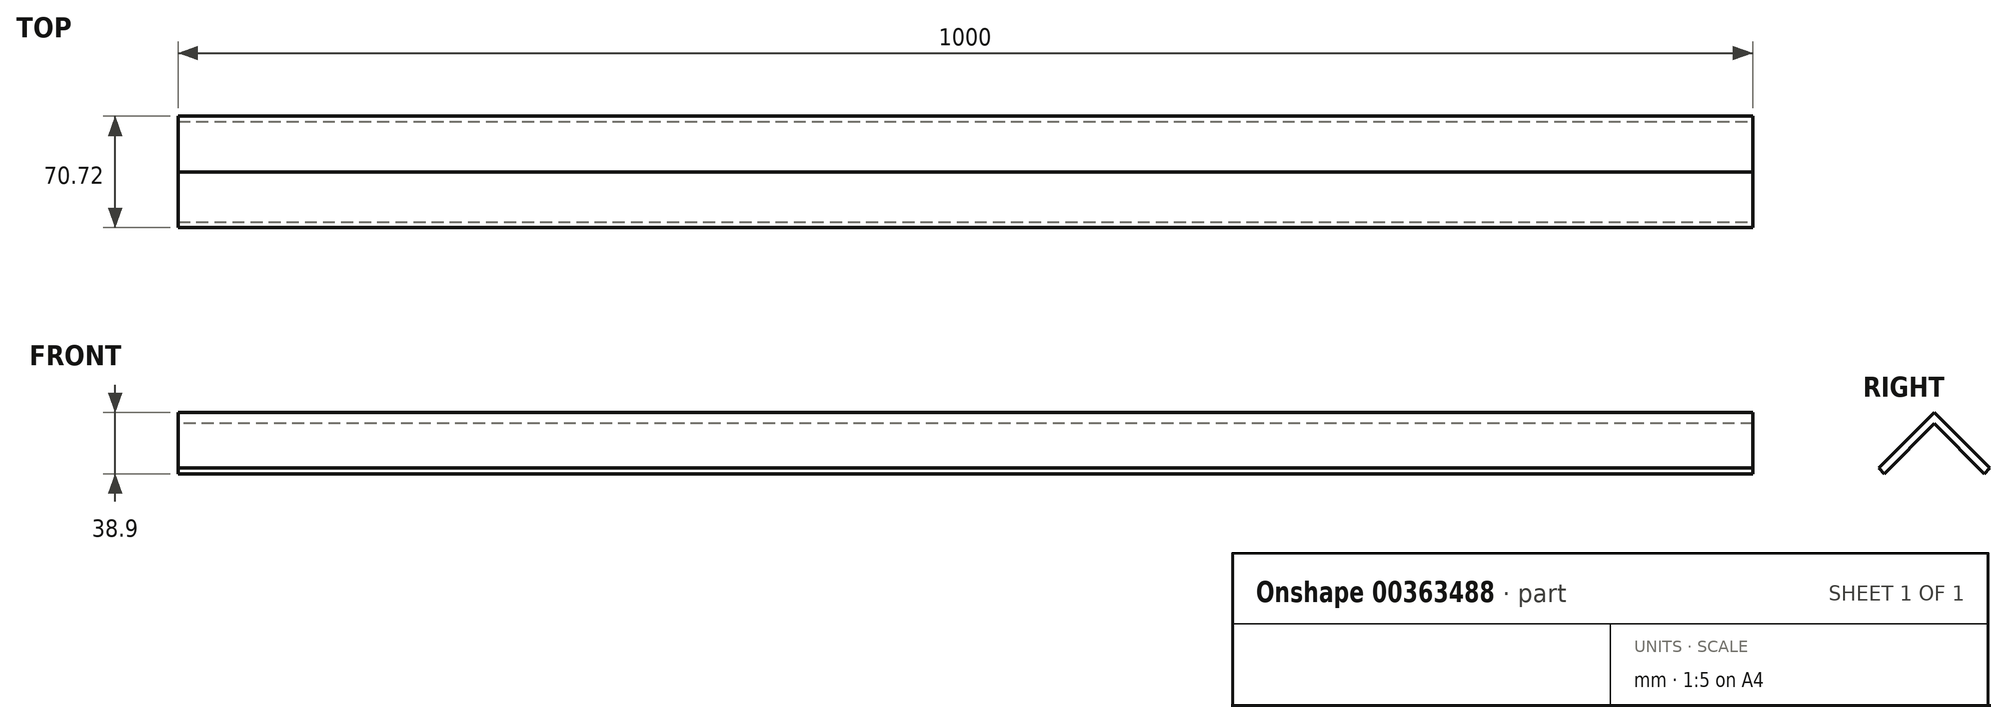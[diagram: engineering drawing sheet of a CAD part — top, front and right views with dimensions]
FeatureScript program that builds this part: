
annotation { "Feature Type Name" : "Feature", "Feature Type Description" : "" }
export const myFeature = defineFeature(function(context is Context, id is Id, definition is map)
    precondition{}
    {
        {
            var Q0;
            Q0=qCreatedBy(makeId("Right.planeOp"),FACE);
            var sketch = newSketch(context, id + "F0", { "sketchPlane" : qUnion([Q0])});
            skLineSegment(sketch, "E0", {"start": v(-35.36, 0) * mm, "end": v(0, 35.36) * mm});
            skLineSegment(sketch, "E1", {"start": v(0, 35.36) * mm, "end": v(35.36, 0) * mm});
            skSolve(sketch);
        }
        {
            var Q0;
            Q0=sQuery(id+"F0.wireOp",EDGE,"E0");
            var Q1;
            Q1=sQuery(id+"F0.wireOp",EDGE,"E1");
            extrude(context, id + "F1", {"bodyType" : ToolBodyType.SURFACE, "surfaceEntities" : qUnion([Q0, Q1]), "depth" : 1000 * mm});
        }
        {
            var Q0;
            Q0=makeQuery(id+"F1.opExtrude","SWEPT_FACE",FACE,{"disambiguationData":[OSD([sQuery(id+"F0.wireOp",EDGE,"E0")])]});
            extrude(context, id + "F2", {"entities" : qUnion([Q0]), "depth" : 5 * mm});
        }
        {
            var Q0;
            Q0=makeQuery(id+"F1.opExtrude","SWEPT_FACE",FACE,{"disambiguationData":[OSD([sQuery(id+"F0.wireOp",EDGE,"E1")])]});
            extrude(context, id + "F3", {"entities" : qUnion([Q0]), "operationType" : NewBodyOperationType.ADD, "depth" : 5 * mm});
        }
    });
